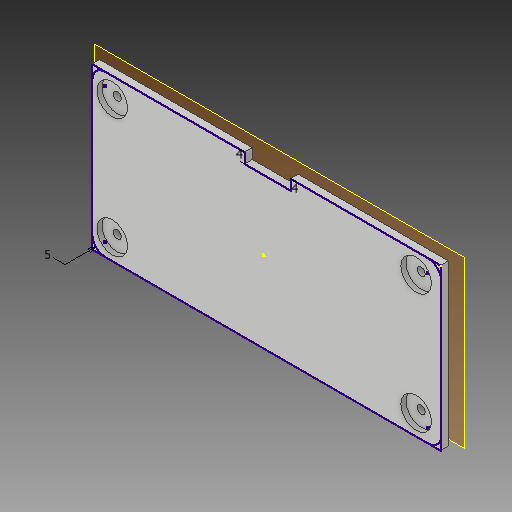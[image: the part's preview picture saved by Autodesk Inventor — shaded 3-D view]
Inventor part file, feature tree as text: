
AUTODESK INVENTOR PART (.ipt)
format: ipt  version: 2019 (Build 230136000, 136)  size: 254,976 bytes
history: native  units: mm
features: sketch x6, reference x6, extrude x5, other x3, plane x2, fillet x1, direct_edit x1, move_body x1
ambient origin geometry x8: Origin, YZ Plane, XZ Plane, XY Plane, X Axis, Y Axis, Z Axis, Center Point
bodies: Volumenkörper1 (feature_tree)
feature tree (25):
  plane  "Arbeitsebene1"
  extrude  "Extrusion1"  Depth=6.0mm
  plane  "Arbeitsebene2"
  extrude  "Extrusion2"  Depth=6.0mm
  extrude  "Extrusion3"  Depth=3.0mm
  fillet  "Rundung1"  Radius=7.0mm
  extrude  "Extrusion5"  Depth=7.0mm
  extrude  "Extrusion6"  Depth=3.0mm
  direct_edit  "Direktbearbeitung1"
  sketch  "Skizze7"  dims[d12=15.0mm d13=15.0mm d14=15.0mm d15=15.0mm d16=5.0mm d17=29.0mm d18=14.0mm d19=20.0mm d20=18.0mm d21=7.0mm d22=7.0mm d23=12.0mm d24=5.0mm d25=13.0mm d26=30.0mm d27=31.0mm d28=3.0mm d29=0.0mm d31=8.0mm d32=8.0mm d33=8.0mm d34=8.0mm d35=3.0mm d36=0.0mm d37=3.75mm d44=12.0mm d45=12.0mm d46=12.0mm d47=12.0mm d48=2.0mm d49=0.0mm d50=1.5mm d51=18.0mm d52=59.0mm d53=4.0mm d54=0.0mm d55=0.0mm d56=0.0mm d57=-2.5mm d58=4.0mm d59=4.0mm d60=5.0mm]
  sketch  "Skizze1"  dims[d0=6.0mm d1=6.0mm]
  reference  "Referenz1"
  reference  "Referenz2"
  reference  "Referenz3"
  reference  "Referenz4"
  sketch  "Skizze2"  dims[d2=6.0mm d3=6.0mm]
  reference  "Referenz5"
  reference  "Referenz6"
  sketch  "Skizze3"  dims[d4=3.0mm d5=0.0mm d6=3.0mm d7=7.0mm]
  sketch  "Skizze5"  dims[d8=7.0mm d9=7.0mm]
  sketch  "Skizze6"  dims[d10=7.0mm d11=3.0mm]
  other  "<userpath>\Google Drive\Projekte\makroboard\makroboard_case\Baugruppe1.iam"
  other  "Baugruppe1.iam"
  other  "makroboard:1"
  move_body  "Verschieben1"
